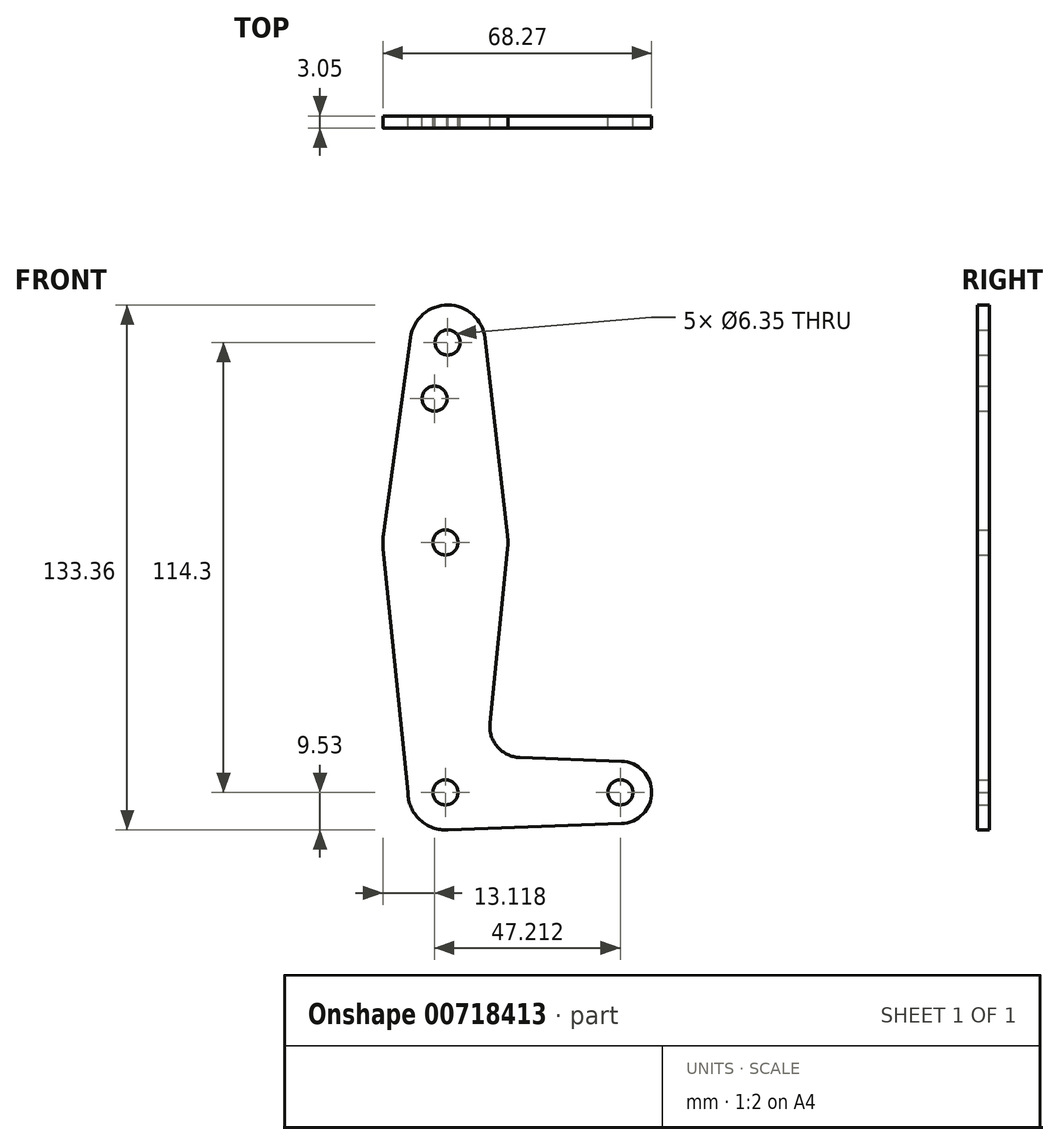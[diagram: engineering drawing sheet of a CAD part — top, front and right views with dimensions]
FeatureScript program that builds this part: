
annotation { "Feature Type Name" : "Feature", "Feature Type Description" : "" }
export const myFeature = defineFeature(function(context is Context, id is Id, definition is map)
    precondition{}
    {
        {
            var Q0;
            Q0=qCreatedBy(makeId("Front.planeOp"),FACE);
            var sketch = newSketch(context, id + "F0", { "sketchPlane" : qUnion([Q0])});
            skLineSegment(sketch, "E0", {"start": v(0, 0) * mm, "end": v(44.45, 0) * mm, "construction": true});
            skCircle(sketch, "E1", {"center": v(0, 63.5) * mm, "radius": 15.88 * mm});
            skCircle(sketch, "E2", {"center": v(44.45, 0) * mm, "radius": 7.94 * mm});
            skCircle(sketch, "E3", {"center": v(0, 0) * mm, "radius": 9.53 * mm});
            skCircle(sketch, "E4", {"center": v(0.57, 114.3) * mm, "radius": 9.53 * mm});
            skLineSegment(sketch, "E5", {"start": v(0, 63.5) * mm, "end": v(0, 0) * mm, "construction": true});
            skLineSegment(sketch, "E6", {"start": v(0, 63.5) * mm, "end": v(0.57, 114.3) * mm, "construction": true});
            skLineSegment(sketch, "E7", {"start": v(11.3, 17.6) * mm, "end": v(16.07, 64.6) * mm});
            skLineSegment(sketch, "E8", {"start": v(-9.53, 0) * mm, "end": v(-16.46, 68.47) * mm});
            skLineSegment(sketch, "E9", {"start": v(15.77, 65.3) * mm, "end": v(10.04, 115.38) * mm});
            skLineSegment(sketch, "E10", {"start": v(-15.73, 65.66) * mm, "end": v(-8.86, 115.6) * mm});
            skLineSegment(sketch, "E11", {"start": v(18.93, 8.85) * mm, "end": v(44.73, 7.93) * mm});
            skLineSegment(sketch, "E12", {"start": v(0, -9.53) * mm, "end": v(44.73, -7.93) * mm});
            skCircle(sketch, "E13", {"center": v(0.57, 114.3) * mm, "radius": 3.18 * mm});
            skCircle(sketch, "E14", {"center": v(0, 63.5) * mm, "radius": 3.18 * mm});
            skCircle(sketch, "E15", {"center": v(0, 0) * mm, "radius": 3.18 * mm});
            skCircle(sketch, "E16", {"center": v(44.45, 0) * mm, "radius": 3.18 * mm});
            skArc(sketch, "E17.filletArc", {"start": v(11.3, 17.6) * mm, "mid": v(13.22, 11.57) * mm, "end": v(18.93, 8.85) * mm});
            skLineSegment(sketch, "E18", {"start": v(-2.76, 100.03) * mm, "end": v(0.41, 100.03) * mm});
            skCircle(sketch, "E19", {"center": v(-2.76, 100.03) * mm, "radius": 3.18 * mm});
            skSolve(sketch);
        }
        {
            var Q0;
            Q0 = qSketchRegion(id + "F0", true);
            extrude(context, id + "F1", {"entities" : qUnion([Q0]), "depth" : 3.05 * mm, "offsetDistance" : 25.4 * mm});
        }
    });
